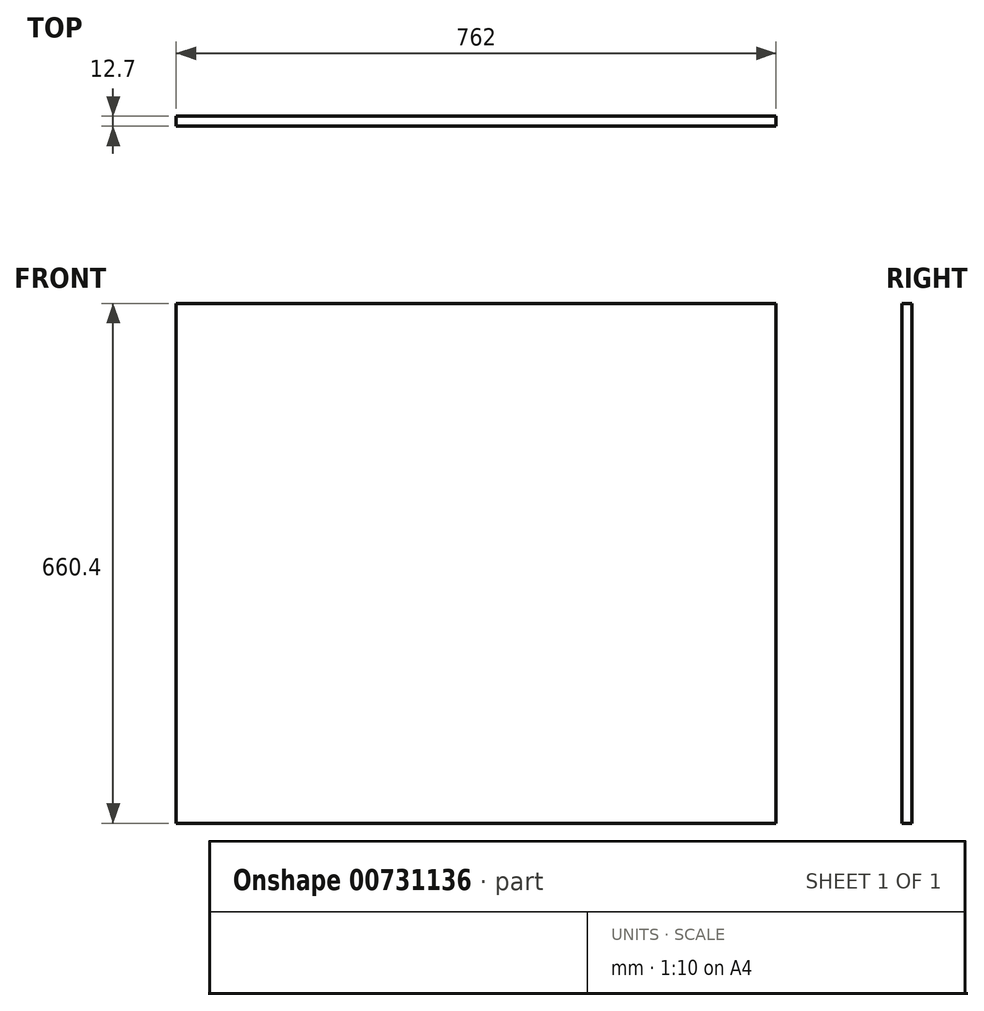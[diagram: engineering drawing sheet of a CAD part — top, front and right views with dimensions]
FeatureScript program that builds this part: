
annotation { "Feature Type Name" : "Feature", "Feature Type Description" : "" }
export const myFeature = defineFeature(function(context is Context, id is Id, definition is map)
    precondition{}
    {
        {
            var Q0;
            Q0=qCreatedBy(makeId("Front.planeOp"),FACE);
            var sketch = newSketch(context, id + "F0", { "sketchPlane" : qUnion([Q0])});
            skLineSegment(sketch, "E0.bottom", {"start": v(381, 330.2) * mm, "end": v(-381, 330.2) * mm});
            skLineSegment(sketch, "E0.top", {"start": v(381, -330.2) * mm, "end": v(-381, -330.2) * mm});
            skLineSegment(sketch, "E0.left", {"start": v(381, 330.2) * mm, "end": v(381, -330.2) * mm});
            skLineSegment(sketch, "E0.right", {"start": v(-381, 330.2) * mm, "end": v(-381, -330.2) * mm});
            skPoint(sketch, "E0.middle", {"position": v(0, 0) * mm});
            skSolve(sketch);
        }
        {
            var Q0;
            Q0 = qSketchRegion(id + "F0", true);
            extrude(context, id + "F1", {"entities" : qUnion([Q0]), "depth" : 12.7 * mm, "offsetDistance" : 25.4 * mm});
        }
    });
